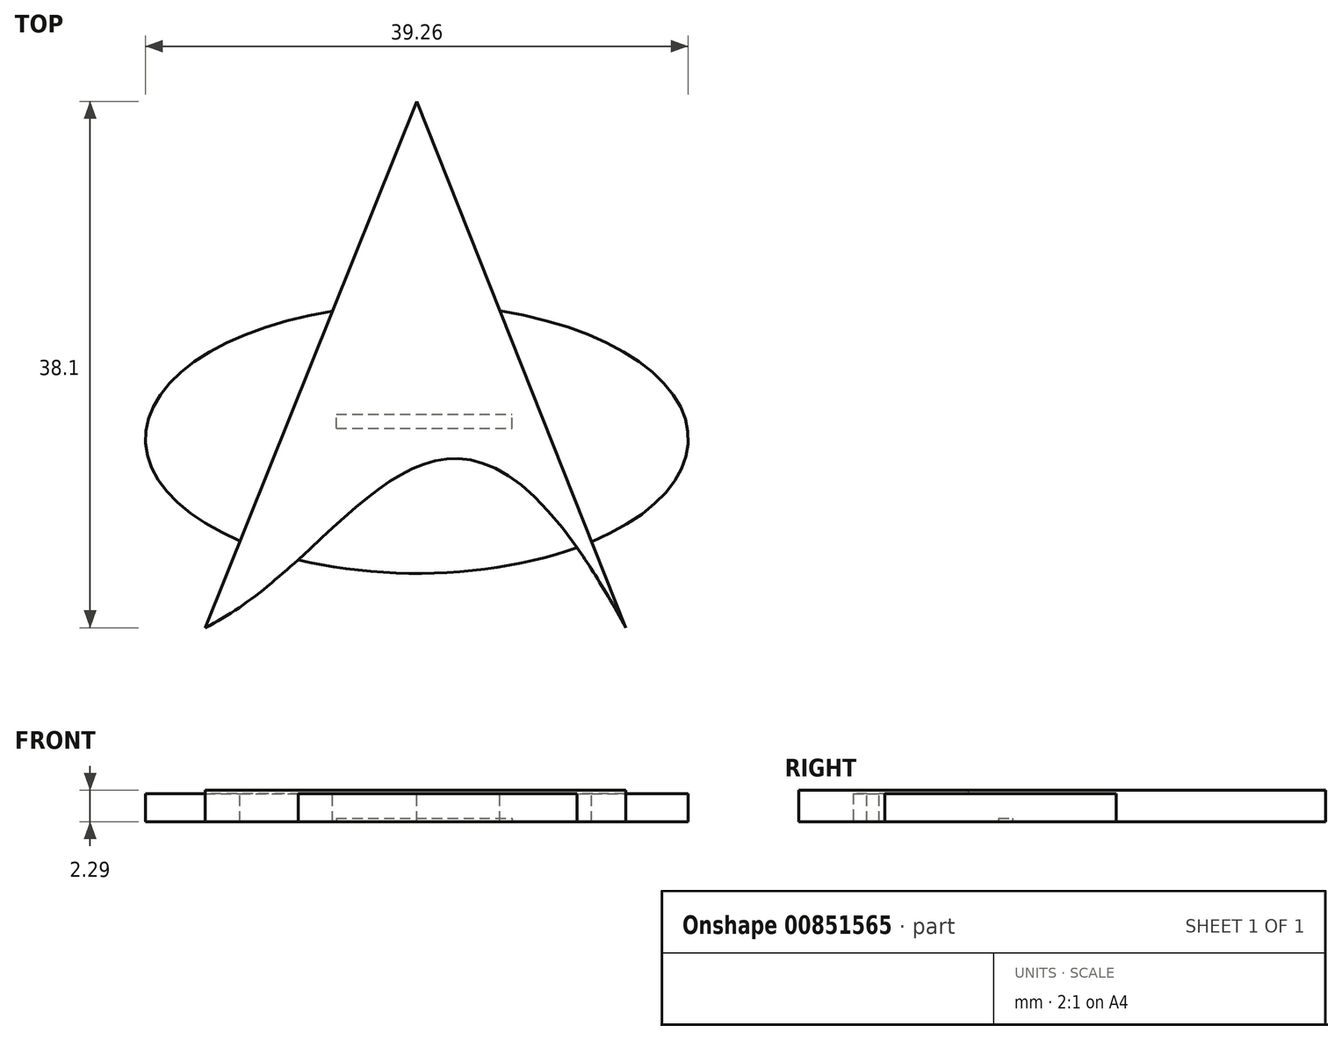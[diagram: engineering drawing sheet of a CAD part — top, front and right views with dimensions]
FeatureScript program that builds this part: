
annotation { "Feature Type Name" : "Feature", "Feature Type Description" : "" }
export const myFeature = defineFeature(function(context is Context, id is Id, definition is map)
    precondition{}
    {
        {
            var Q0;
            Q0=qCreatedBy(makeId("Top.planeOp"),FACE);
            var sketch = newSketch(context, id + "F0", { "sketchPlane" : qUnion([Q0])});
            skLineSegment(sketch, "E0", {"start": v(-15.69, -13.48) * mm, "end": v(-0.37, 24.62) * mm});
            skLineSegment(sketch, "E1", {"start": v(-0.37, 24.62) * mm, "end": v(14.73, -13.48) * mm});
            skFitSpline(sketch, "E2", {"points": [v(-15.69, -13.48) * mm, v(14.73, -13.48) * mm], "startDerivative": vector(34.1, 16.86) * mm, "endDerivative": vector(39.35, -73.55) * mm});
            skEllipticalArc(sketch, "E3", {});
            skEllipticalArc(sketch, "E4.trimOffspring", {});
            skEllipticalArc(sketch, "E5.trimOffspring", {});
            const initialGuessF0  = {"E3": [-0.0003707793305433579, 0.00019240255326164867, 1, 0, 0.019631532065344785, 0.009730761957063877, 5.411569815407148, 1.2596500863328615], "E4.trimOffspring": [-0.0003707793305433579, 0.00019240255326164867, 1, 0, 0.019631532065344785, 0.009730761957063877, 4.2596733084288925, 5.34322991153381], "E5.trimOffspring": [-0.0003707793305433579, 0.00019240255326164867, 1, 0, 0.019631532065344785, 0.009730761957063877, 1.8867642181982716, 4.0030869742612545]};
            skSetInitialGuess(sketch, initialGuessF0);
            skSolve(sketch);
        }
        {
            var Q0;
            Q0 = qSketchRegion(id + "F0", true);
            var Q1;
            Q1 = qConstructionFilter(qBodyType(qCreatedBy(id + "F0" ,EDGE), BodyType.WIRE), ConstructionObject.NO);
            extrude(context, id + "F1", {"entities" : qUnion([Q0]), "surfaceEntities" : qUnion([Q1]), "oppositeDirection" : true, "depth" : 2.3 * mm, "offsetDistance" : 25.4 * mm});
        }
        {
            var Q0;
            {var subQ0=sQuery(id+"F0.wireOp",EDGE,"E5.trimOffspring");Q0=makeQuery(id+"F0.imprint","IMPRINT",FACE,{"disambiguationData":[TD([[makeQuery(id+"F0.imprint","IMPRINT",EDGE,{"derivedFrom":subQ0}),1.0]])]});}
            var Q1;
            {var subQ0=sQuery(id+"F0.wireOp",EDGE,"E3");Q1=makeQuery(id+"F0.imprint","IMPRINT",FACE,{"disambiguationData":[TD([[makeQuery(id+"F0.imprint","IMPRINT",EDGE,{"derivedFrom":subQ0}),1.0]])]});}
            var Q2;
            {var subQ0=sQuery(id+"F0.wireOp",EDGE,"E4.trimOffspring");Q2=makeQuery(id+"F0.imprint","IMPRINT",FACE,{"disambiguationData":[TD([[makeQuery(id+"F0.imprint","IMPRINT",EDGE,{"derivedFrom":subQ0}),1.0]])]});}
            extrude(context, id + "F2", {"entities" : qUnion([Q0, Q1, Q2]), "operationType" : NewBodyOperationType.REMOVE, "oppositeDirection" : true, "depth" : 0.25 * mm, "offsetDistance" : 25.4 * mm});
        }
        {
            var Q0;
            Q0=makeQuery(id+"F1.opExtrude","CAP_FACE",FACE,{"disambiguationData":[OSD([sQuery(id+"F0.wireOp",EDGE,"E0"),sQuery(id+"F0.wireOp",EDGE,"E1"),sQuery(id+"F0.wireOp",EDGE,"E2"),sQuery(id+"F0.wireOp",EDGE,"E3"),sQuery(id+"F0.wireOp",EDGE,"E4.trimOffspring"),sQuery(id+"F0.wireOp",EDGE,"E5.trimOffspring")])],"isStart":false});
            var sketch = newSketch(context, id + "F3", { "sketchPlane" : qUnion([Q0])});
            skLineSegment(sketch, "E6.bottom", {"start": v(-6.19, -0.96) * mm, "end": v(6.51, -0.96) * mm});
            skLineSegment(sketch, "E6.top", {"start": v(-6.19, -1.98) * mm, "end": v(6.51, -1.98) * mm});
            skLineSegment(sketch, "E6.left", {"start": v(-6.19, -0.96) * mm, "end": v(-6.19, -1.98) * mm});
            skLineSegment(sketch, "E6.right", {"start": v(6.51, -0.96) * mm, "end": v(6.51, -1.98) * mm});
            skSolve(sketch);
        }
        {
            var Q0;
            Q0 = qSketchRegion(id + "F3", true);
            extrude(context, id + "F4", {"entities" : qUnion([Q0]), "operationType" : NewBodyOperationType.REMOVE, "oppositeDirection" : true, "depth" : 0.25 * mm, "offsetDistance" : 25.4 * mm});
        }
    });
